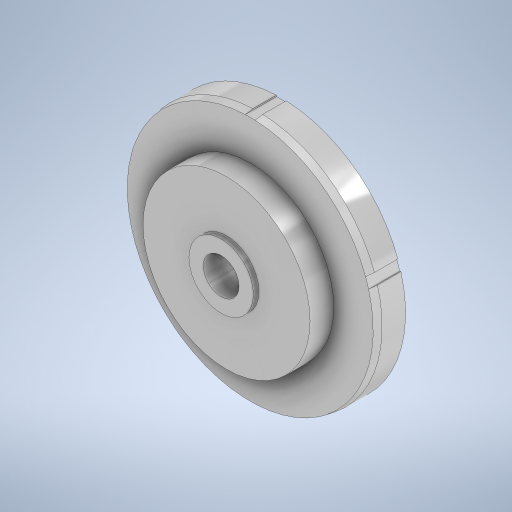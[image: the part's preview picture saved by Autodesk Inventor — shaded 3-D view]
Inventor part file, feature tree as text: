
AUTODESK INVENTOR PART (.ipt)
format: ipt  version: 2023 (Build 270158000, 158)  size: 337,408 bytes
history: native  units: mm
features: extrude x5, sketch x5, chamfer x1
ambient origin geometry x8: Origin, YZ Plane, XZ Plane, XY Plane, X Axis, Y Axis, Z Axis, Center Point
bodies: Solid1 (feature_tree)
feature tree (11):
  extrude  "Extrusion1"  Depth=0.55mm
  chamfer  "Chamfer1"  Distance=50.0mm Angle=360.0deg
  extrude  "Extrusion2"  Depth=13.0mm TaperAngle=45.0deg
  extrude  "Extrusion3"  Depth=4.0mm TaperAngle=0.0deg
  extrude  "Extrusion4"  Depth=2.25mm
  extrude  "Extrusion5"  Depth=9.9mm TaperAngle=0.0deg
  sketch  "Sketch1"  dims[d0=104.05mm d2=0.55mm]
  sketch  "Sketch2"  dims[d3=2.05mm]
  sketch  "Sketch3"  dims[d4=4.1mm d5=50.0mm d7=360.0deg]
  sketch  "Sketch4"  dims[d9=13.0mm d10=0.0mm d11=0.55mm d12=3.2mm d13=45.0deg]
  sketch  "Sketch5"  dims[d14=44.0mm d15=4.0mm d16=0.0mm d17=69.9mm d18=9.9mm d19=0.0mm d20=27.0mm d21=2.25mm d22=0.0mm d23=15.0mm d24=0.0mm d25=0.0mm]
